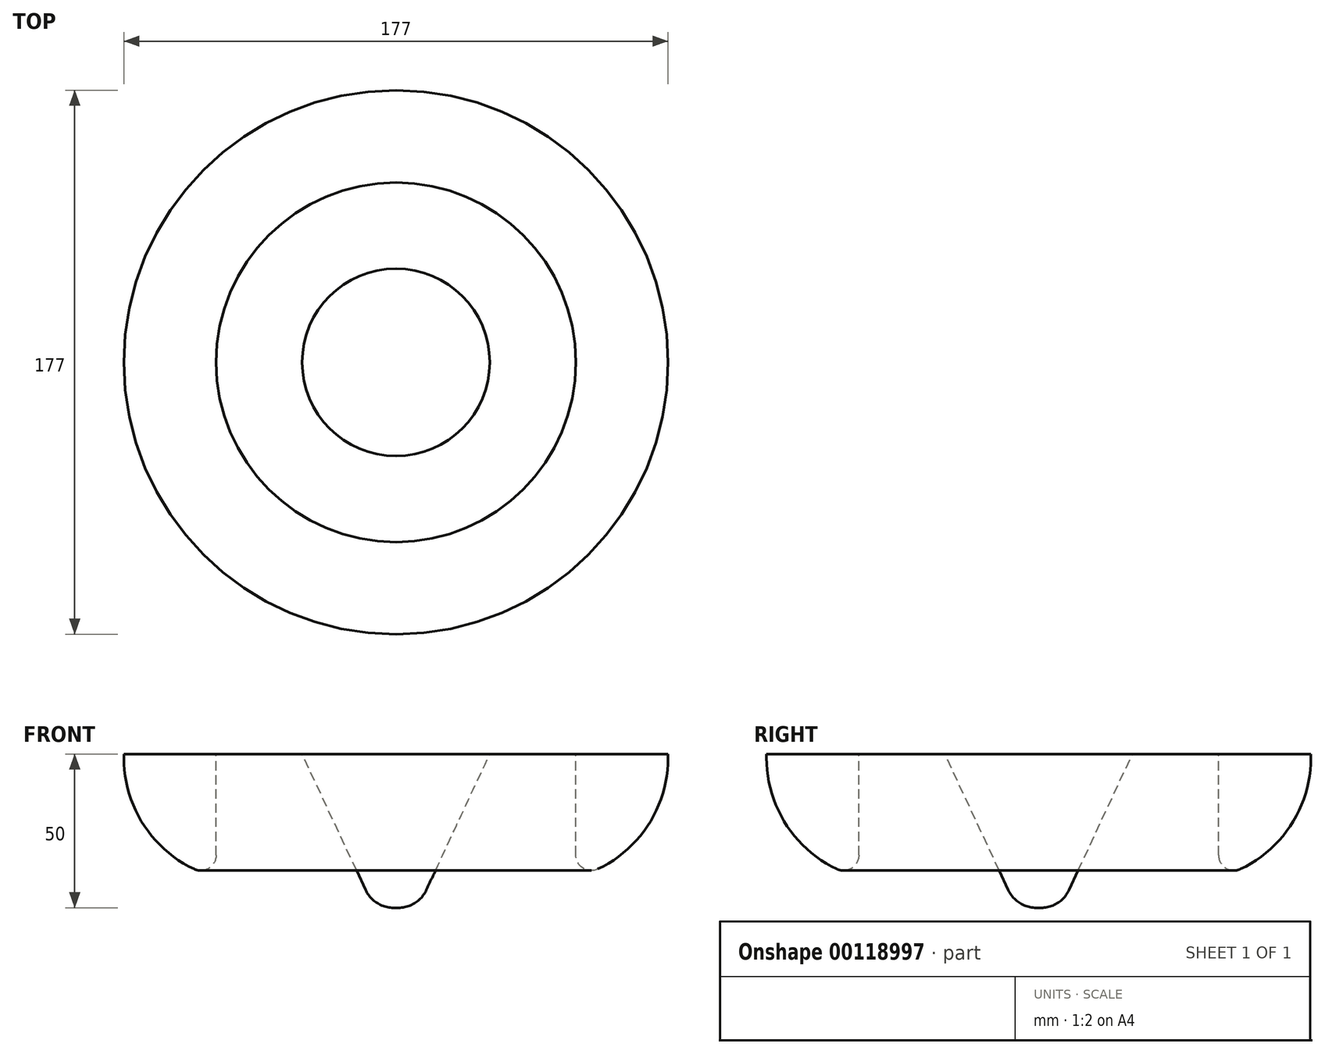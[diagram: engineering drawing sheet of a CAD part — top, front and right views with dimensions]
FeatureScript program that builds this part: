
annotation { "Feature Type Name" : "Feature", "Feature Type Description" : "" }
export const myFeature = defineFeature(function(context is Context, id is Id, definition is map)
    precondition{}
    {
        {
            var Q0;
            Q0=qCreatedBy(makeId("Top.planeOp"),FACE);
            var sketch = newSketch(context, id + "F0", { "sketchPlane" : qUnion([Q0])});
            skCircle(sketch, "E0", {"center": v(0, 0) * mm, "radius": 30.5 * mm});
            skCircle(sketch, "E1", {"center": v(0, 0) * mm, "radius": 88.5 * mm});
            skCircle(sketch, "E2", {"center": v(0, 0) * mm, "radius": 58.5 * mm});
            skSolve(sketch);
        }
        {
            var Q0;
            Q0=makeQuery(id+"F0.imprint","IMPRINT",FACE,{"disambiguationData":[TD([[makeQuery(id+"F0.imprint","IMPRINT",EDGE,{"derivedFrom":sQuery(id+"F0.wireOp",EDGE,"E0")}),1.0]])]});
            extrude(context, id + "F1", {"entities" : qUnion([Q0]), "oppositeDirection" : true, "depth" : 50 * mm, "hasDraft" : true, "draftAngle" : 25 * degree, "draftPullDirection" : true});
        }
        {
            var Q0;
            Q0=makeQuery(id+"F1.opExtrude","CAP_FACE",FACE,{"disambiguationData":[OSD([sQuery(id+"F0.wireOp",EDGE,"E0")])],"isStart":false});
            fillet(context, id + "F2", {"entities" : qUnion([Q0]), "radius" : 10 * mm, "tangentPropagation" : true, "allowEdgeOverflow" : false});
        }
        {
            var Q0;
            Q0 = qSketchRegion(id + "F0", true);
            extrude(context, id + "F3", {"entities" : qUnion([Q0]), "oppositeDirection" : true, "depth" : 40 * mm});
        }
        {
            var Q0;
            Q0=makeQuery(id+"F3.opExtrude","CAP_EDGE",EDGE,{"disambiguationData":[OSD([sQuery(id+"F0.wireOp",EDGE,"E1")])],"isStart":false});
            fillet(context, id + "F4", {"entities" : qUnion([Q0]), "radius" : 40 * mm, "tangentPropagation" : true, "allowEdgeOverflow" : false});
        }
        {
            var Q0;
            Q0=makeQuery(id+"F4.opFillet","BLEND_EDGE",EDGE,{"blendedFrom":[makeQuery(id+"F3.opExtrude","CAP_EDGE",EDGE,{"disambiguationData":[OSD([sQuery(id+"F0.wireOp",EDGE,"E1")])],"isStart":false}),makeQuery(id+"F3.opExtrude","SWEPT_FACE",FACE,{"disambiguationData":[OSD([sQuery(id+"F0.wireOp",EDGE,"E2")])]})],"blendedInto":[makeQuery(id+"F3.opExtrude","SWEPT_FACE",FACE,{"disambiguationData":[OSD([sQuery(id+"F0.wireOp",EDGE,"E2")])]})]});
            fillet(context, id + "F5", {"entities" : qUnion([Q0]), "radius" : 5 * mm, "tangentPropagation" : true, "allowEdgeOverflow" : false});
        }
    });
